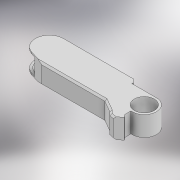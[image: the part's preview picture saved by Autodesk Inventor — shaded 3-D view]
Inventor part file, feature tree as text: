
AUTODESK INVENTOR PART (.ipt)
format: ipt  version: 2022 (Build 260153000, 153)  size: 220,672 bytes
history: native  units: mm
features: sketch x6, extrude x5, fillet x2, chamfer x2, plane x1
ambient origin geometry x8: Origin, YZ Plane, XZ Plane, XY Plane, X Axis, Y Axis, Z Axis, Center Point
bodies: Solid1 (feature_tree)
feature tree (16):
  extrude  "Extrusion1"  Depth=5.5mm
  plane  "Work Plane1"
  sketch  "Sketch2"  dims[d2=24.43461mm d3=1.5mm]
  extrude  "Extrusion2"  Depth=1.5mm
  extrude  "Extrusion3"  Depth=1.25mm
  extrude  "Extrusion4"  Depth=1.0mm
  extrude  "Extrusion5"  Depth=1.0mm
  fillet  "Fillet1"  Radius=2.0mm
  chamfer  "Chamfer1"  Distance=6.0mm
  chamfer  "Chamfer2"  Distance=5.95mm
  fillet  "Fillet2"  Radius=5.083mm
  sketch  "Sketch1"  dims[d0=7.25mm d1=5.5mm]
  sketch  "Sketch3"  dims[d4=1.8mm d5=1.25mm]
  sketch  "Sketch4"  dims[d6=0.25mm d7=1.0mm]
  sketch  "Sketch5"  dims[d8=1.0mm d9=3.5mm d10=2.0mm]
  sketch  "Sketch6"  dims[d11=19.0mm d12=6.0mm d13=5.95mm d14=0.0mm d15=5.083mm d16=7.5mm d17=5.0mm d18=8.25mm d19=0.0mm d20=5.1mm d21=5.0mm d22=0.0mm d23=3.5mm d24=4.25mm d25=0.0mm d26=2.0mm d27=4.25mm d28=0.0mm d29=0.3665mm d30=0.5mm d31=2.0mm d32=45.0deg d33=1.0mm d34=2.0mm d35=45.0deg d36=1.0mm]
